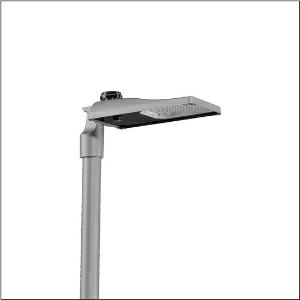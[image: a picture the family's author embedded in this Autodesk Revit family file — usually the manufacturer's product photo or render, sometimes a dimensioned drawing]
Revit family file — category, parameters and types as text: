
# Revit family: streetlight_sl_31_mini___st1_0a_5xh2d3bm08ga_d23b
name_source: partatom
category: Lighting Fixtures
units: mm (PartAtom-declared; Revit-internal decimal feet)

## family parameters
Cut with Voids When Loaded = No
Host = Face
Light Source = No
Part Type = Normal
Room Calculation Point = No
Round Connector Dimension = Use Diameter
Shared = No

## types (1)
- --- (1 x LED, 5880 lm, 39.3 W, 3000K)
    Apparent Load = 39 VA
    CIE Flux Codes = 37 72 97 100 100
    Color Rendering = 70
    Color Temperature = 3000K
    Default Elevation = 1800 mm
    Description = Streetlight SL 31 mini, mast luminaire, primary light control with lens, of PMMA, primary optical cover: cover, of toughened safety glass, transparent, light distribution: ST1.0a, light emission: direct distribution, primary light characteristic: asymmetric, installation type: post-top, side-entry, LED, High Power LED, rated luminous flux: 5.880lm, luminous efficacy: 150lm/W, light colour: 730, colour temperature: 3000K, control: presetting dimming linear, flexible luminous flux parameterisation, time-dependent luminous flux control, constant luminous flux control, intelligent temperature release in ECG and LED module, overheat protection, with cable H07RN-F 3x 1.5mm², mains connection: 220..240V, AC, 50/60Hz, connection cable pre-assembled, cable length: 6,5m, start of lifetime: 39W, end of service life: 41W, reduction: 18W, luminaire housing, of diecast aluminium, powder-coated, Siteco® metallic grey (DB 702S), corrosivity category C5 high according to DIN EN ISO 12944, no sealing on luminaire upper side, inclination: -15°..+20° (post-top) | -20°..+20° (side-entry), adjustable in 5° steps, mast flange (76/60mm) included as standard, multi-level sealing system, sealing non-destructively replaceable, Smart Interface below, protection rating (complete): IP66, insulation class (complete): insulation class I (protective earthing), certification: CE, ENEC, ENEC+, VDE, UKCA, impact resistance: IK09, permissible operating ambient temperature for outdoor applications: -40..+50°C, standard-compliant lighting for roads and squares, packaging unit: 1 piece

Light Distribution: ST1.0a
    Height = 76 mm
    Lamp = 1 x LED
    Lamp Light Flux = 5880 lm
    Lamp Power = 39.3 W
    Lamp count = 1
    Length = 547 mm
    Luminous efficacy = 150 lm/W
    Manufacturer = Siteco
    ModVariant = No
    Model = 5XH2D3BM08GA
    Number of Poles = 1
    OnlyDefault = Yes
    Power Factor = 1
    Product Name = Streetlight SL 31 mini | ST1.0a
    Product group = mast luminaire | pylon top
    ProductGroupID = 6100
    Protection Class = Protection class I
    Protection Degree = IP 66
    RLX_Detail_Level = 1
    RLX_Emergency_Light_Flux = 0 lm
    RLX_Emergency_Type = 0
    RLX_Emergency_Type_DB = No
    RlxData = <blob elided: 40629 chars, md5=424f832d>
    Socket = socket
    Standby Power = 0 W
    System Light Flux = 5880 lm
    System Power = 39 W
    Type Comments = factory setting: luminous flux: 100 % | dim-lin: 254 | 798 mA
    Type Image = l_1300324.jpg
    URL = http://relux.com
    VarID = @adj_012493
    Voltage = 0 V
    Weight = 0.00 kg
    Width = 265 mm

## geometry (parser evidence)
native form markers: Blend x4, Sweep x11
no freeform markers — native parametric forms only
